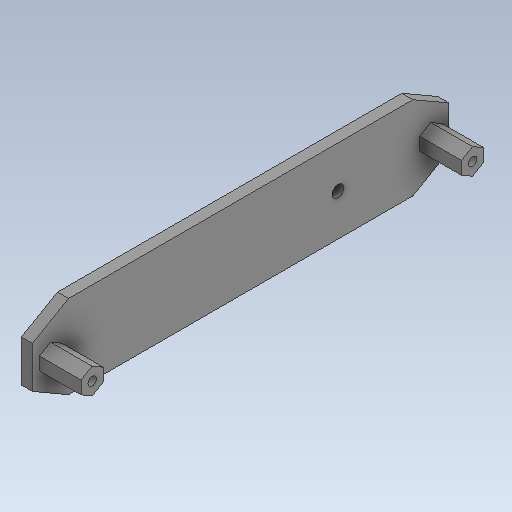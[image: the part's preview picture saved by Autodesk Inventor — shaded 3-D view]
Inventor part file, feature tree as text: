
AUTODESK INVENTOR PART (.ipt)
format: ipt  version: 2020 (Build 240168000, 168)  size: 259,584 bytes
history: native  units: in
note: dims shown in document units (in); Inventor stores cm internally (conversion verified against a paired STEP export)
features: extrude x6, sketch x6, plane x1
ambient origin geometry x8: Origin, YZ Plane, XZ Plane, XY Plane, X Axis, Y Axis, Z Axis, Center Point
bodies: Solid1 (feature_tree)
feature tree (13):
  extrude  "Extrusion1"  Depth=5.9055in
  extrude  "Extrusion3"  TaperAngle=0.0deg  [1 undecoded]
  extrude  "Extrusion4"  Depth=0.5906in
  plane  "Work Plane1"
  extrude  "Extrusion5"  Depth=0.122in
  extrude  "Extrusion6"  Depth=0.2402in
  extrude  "Extrusion7"  [1 undecoded]
  sketch  "Sketch1"  dims[d0=1.1811in d1=5.9055in]
  sketch  "Sketch2"  dims[d2=0.1575in d3=0.0in]
  sketch  "Sketch3"  dims[d8=0.315in d9=0.5906in]
  sketch  "Sketch4"  dims[d10=0.0in d12=0.122in]
  sketch  "Sketch5"  dims[d13=0.0in d14=0.0in d15=0.2402in]
  sketch  "Sketch8"  dims[d16=0.0866in d17=-0.2233in d18=-0.3937in d19=0.0866in d20=0.0in d26=1.5748in d27=0.1654in d30=0.0in d31=0.0in]
note: 2 required parameter values undecoded (feature->parameter linkage not recoverable at this tier; creation-order binding heuristic only, values carry confidence <= 0.55)
